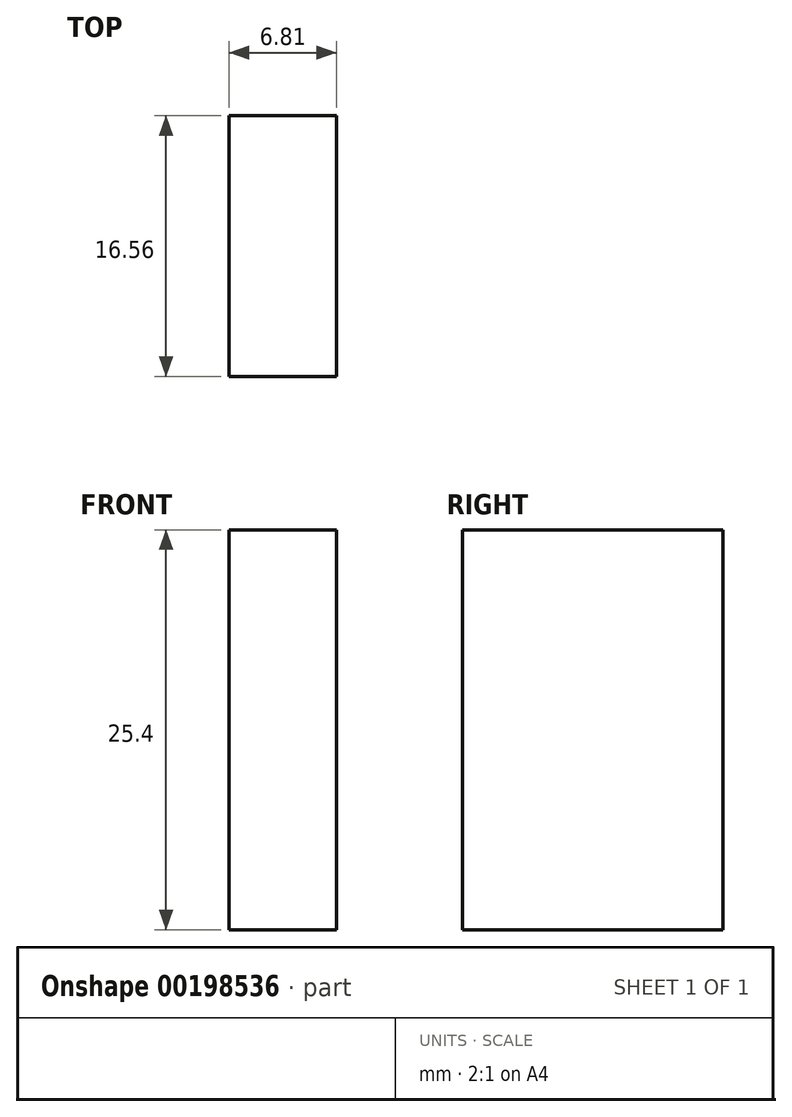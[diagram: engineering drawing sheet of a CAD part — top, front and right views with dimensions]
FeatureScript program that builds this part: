
annotation { "Feature Type Name" : "Feature", "Feature Type Description" : "" }
export const myFeature = defineFeature(function(context is Context, id is Id, definition is map)
    precondition{}
    {
        {
            var Q0;
            Q0=qCreatedBy(makeId("Top.planeOp"),FACE);
            var sketch = newSketch(context, id + "F0", { "sketchPlane" : qUnion([Q0])});
            skLineSegment(sketch, "E0.bottom", {"start": v(0, 16.56) * mm, "end": v(6.8, 16.56) * mm});
            skLineSegment(sketch, "E0.top", {"start": v(0, 0) * mm, "end": v(6.8, 0) * mm});
            skLineSegment(sketch, "E0.left", {"start": v(0, 16.56) * mm, "end": v(0, 0) * mm});
            skLineSegment(sketch, "E0.right", {"start": v(6.8, 16.56) * mm, "end": v(6.8, 0) * mm});
            skSolve(sketch);
        }
        {
            var Q0;
            Q0=makeQuery(id+"F0.imprint","IMPRINT",FACE,{"disambiguationData":[TD([[makeQuery(id+"F0.imprint","IMPRINT",EDGE,{"derivedFrom":sQuery(id+"F0.wireOp",EDGE,"E0.bottom")}),-1.0]])]});
            extrude(context, id + "F1", {"entities" : qUnion([Q0]), "depth" : 25.4 * mm});
        }
    });
